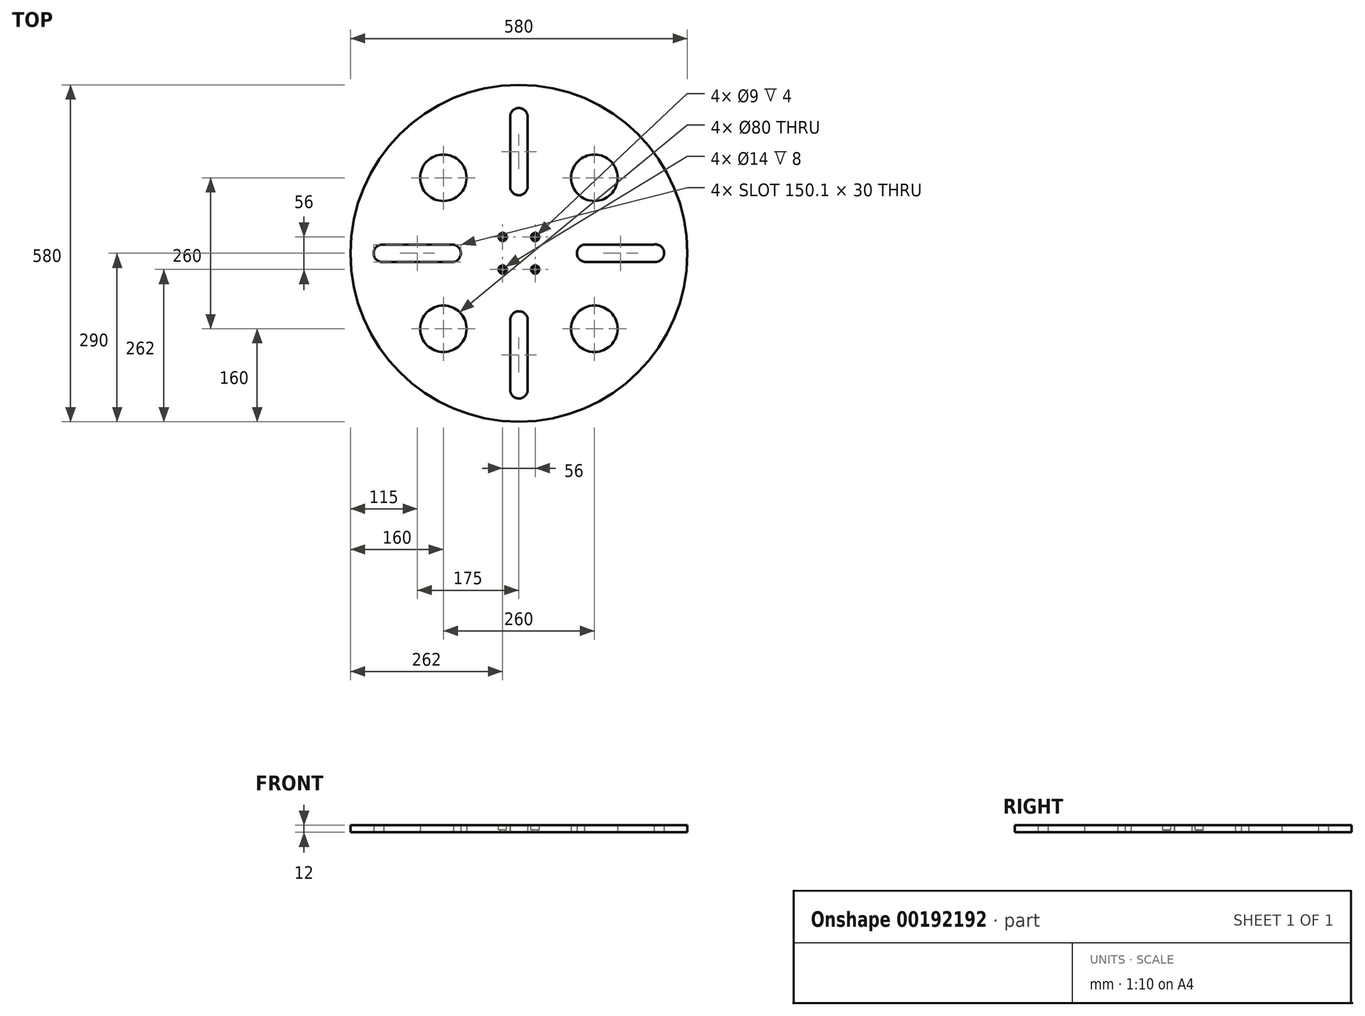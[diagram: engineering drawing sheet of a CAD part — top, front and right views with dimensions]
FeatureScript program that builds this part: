
annotation { "Feature Type Name" : "Feature", "Feature Type Description" : "" }
export const myFeature = defineFeature(function(context is Context, id is Id, definition is map)
    precondition{}
    {
        {
            var Q0;
            Q0=qCreatedBy(makeId("Top.planeOp"),FACE);
            var sketch = newSketch(context, id + "F0", { "sketchPlane" : qUnion([Q0])});
            skCircle(sketch, "E0", {"center": v(0, 0) * mm, "radius": 290 * mm});
            skLineSegment(sketch, "E1.bottom", {"start": v(-115, 15) * mm, "end": v(-235, 15) * mm});
            skLineSegment(sketch, "E1.top", {"start": v(-112.5, -15) * mm, "end": v(-232.5, -15) * mm});
            skPoint(sketch, "E1.middle", {"position": v(-173.75, 0) * mm});
            skArc(sketch, "E2", {"start": v(-235, 15) * mm, "mid": v(-250.05, -1.35) * mm, "end": v(-232.5, -15) * mm});
            skArc(sketch, "E3", {"start": v(-115, 15) * mm, "mid": v(-99.95, 1.15) * mm, "end": v(-112.5, -15) * mm});
            skPoint(sketch, "E4.1.0", {"position": v(0, 173.75) * mm});
            skArc(sketch, "E4.1.1", {"start": v(15, 115) * mm, "mid": v(1.15, 99.95) * mm, "end": v(-15, 112.5) * mm});
            skArc(sketch, "E4.1.2", {"start": v(15, 235) * mm, "mid": v(-1.35, 250.05) * mm, "end": v(-15, 232.5) * mm});
            skLineSegment(sketch, "E4.1.3", {"start": v(-15, 112.5) * mm, "end": v(-15, 232.5) * mm});
            skLineSegment(sketch, "E4.1.4", {"start": v(15, 115) * mm, "end": v(15, 235) * mm});
            skPoint(sketch, "E4.2.0", {"position": v(173.75, 0) * mm});
            skArc(sketch, "E4.2.1", {"start": v(115, -15) * mm, "mid": v(99.95, -1.15) * mm, "end": v(112.5, 15) * mm});
            skArc(sketch, "E4.2.2", {"start": v(235, -15) * mm, "mid": v(250.05, 1.35) * mm, "end": v(232.5, 15) * mm});
            skLineSegment(sketch, "E4.2.3", {"start": v(112.5, 15) * mm, "end": v(232.5, 15) * mm});
            skLineSegment(sketch, "E4.2.4", {"start": v(115, -15) * mm, "end": v(235, -15) * mm});
            skPoint(sketch, "E4.3.0", {"position": v(0, -173.75) * mm});
            skArc(sketch, "E4.3.1", {"start": v(-15, -115) * mm, "mid": v(-1.15, -99.95) * mm, "end": v(15, -112.5) * mm});
            skArc(sketch, "E4.3.2", {"start": v(-15, -235) * mm, "mid": v(1.35, -250.05) * mm, "end": v(15, -232.5) * mm});
            skLineSegment(sketch, "E4.3.3", {"start": v(15, -112.5) * mm, "end": v(15, -232.5) * mm});
            skLineSegment(sketch, "E4.3.4", {"start": v(-15, -115) * mm, "end": v(-15, -235) * mm});
            skCircle(sketch, "E5", {"center": v(-130, 130) * mm, "radius": 40 * mm});
            skCircle(sketch, "E6.MirrorC", {"center": v(130, 130) * mm, "radius": 40 * mm});
            skCircle(sketch, "E7.MirrorC", {"center": v(130, -130) * mm, "radius": 40 * mm});
            skCircle(sketch, "E8.MirrorC", {"center": v(-130, -130) * mm, "radius": 40 * mm});
            skCircle(sketch, "E9", {"center": v(28, 28) * mm, "radius": 4.5 * mm});
            skCircle(sketch, "E10.MirrorC", {"center": v(-28, 28) * mm, "radius": 4.5 * mm});
            skCircle(sketch, "E11.MirrorC", {"center": v(-28, -28) * mm, "radius": 4.5 * mm});
            skCircle(sketch, "E12.MirrorC", {"center": v(28, -28) * mm, "radius": 4.5 * mm});
            skSolve(sketch);
        }
        {
            var Q0;
            Q0=makeQuery(id+"F0.imprint","IMPRINT",FACE,{"disambiguationData":[TD([[makeQuery(id+"F0.imprint","IMPRINT",EDGE,{"derivedFrom":sQuery(id+"F0.wireOp",EDGE,"E0")}),1.0]])]});
            extrude(context, id + "F1", {"entities" : qUnion([Q0]), "depth" : 12 * mm});
        }
        {
            var Q0;
            Q0 = qSketchRegion(id + "F0", true);
            extrude(context, id + "F2", {"entities" : qUnion([Q0]), "operationType" : NewBodyOperationType.REMOVE, "oppositeDirection" : true, "depth" : 25 * mm});
        }
        {
            var Q0;
            Q0=makeQuery(id+"F1.opExtrude","CAP_FACE",FACE,{"disambiguationData":[OSD([sQuery(id+"F0.wireOp",EDGE,"E0"),sQuery(id+"F0.wireOp",EDGE,"E1.bottom"),sQuery(id+"F0.wireOp",EDGE,"E1.top"),sQuery(id+"F0.wireOp",EDGE,"E2"),sQuery(id+"F0.wireOp",EDGE,"E3"),sQuery(id+"F0.wireOp",EDGE,"E4.1.1"),sQuery(id+"F0.wireOp",EDGE,"E4.1.2"),sQuery(id+"F0.wireOp",EDGE,"E4.1.3"),sQuery(id+"F0.wireOp",EDGE,"E4.1.4"),sQuery(id+"F0.wireOp",EDGE,"E4.2.1"),sQuery(id+"F0.wireOp",EDGE,"E4.2.2"),sQuery(id+"F0.wireOp",EDGE,"E4.2.3"),sQuery(id+"F0.wireOp",EDGE,"E4.2.4"),sQuery(id+"F0.wireOp",EDGE,"E4.3.1"),sQuery(id+"F0.wireOp",EDGE,"E4.3.2"),sQuery(id+"F0.wireOp",EDGE,"E4.3.3"),sQuery(id+"F0.wireOp",EDGE,"E4.3.4"),sQuery(id+"F0.wireOp",EDGE,"E5"),sQuery(id+"F0.wireOp",EDGE,"E6.MirrorC"),sQuery(id+"F0.wireOp",EDGE,"E7.MirrorC"),sQuery(id+"F0.wireOp",EDGE,"E8.MirrorC"),sQuery(id+"F0.wireOp",EDGE,"E9"),sQuery(id+"F0.wireOp",EDGE,"E10.MirrorC"),sQuery(id+"F0.wireOp",EDGE,"E11.MirrorC"),sQuery(id+"F0.wireOp",EDGE,"E12.MirrorC")])],"isStart":false});
            var sketch = newSketch(context, id + "F3", { "sketchPlane" : qUnion([Q0])});
            skCircle(sketch, "E13.0", {"center": v(-28, 28) * mm, "radius": 7 * mm});
            skCircle(sketch, "E14.MirrorC", {"center": v(28, 28) * mm, "radius": 7 * mm});
            skCircle(sketch, "E15.MirrorC", {"center": v(-28, -28) * mm, "radius": 7 * mm});
            skCircle(sketch, "E16.MirrorC", {"center": v(28, -28) * mm, "radius": 7 * mm});
            skSolve(sketch);
        }
        {
            var Q0;
            Q0 = qSketchRegion(id + "F3", true);
            extrude(context, id + "F4", {"entities" : qUnion([Q0]), "operationType" : NewBodyOperationType.REMOVE, "oppositeDirection" : true, "depth" : 8 * mm});
        }
    });
